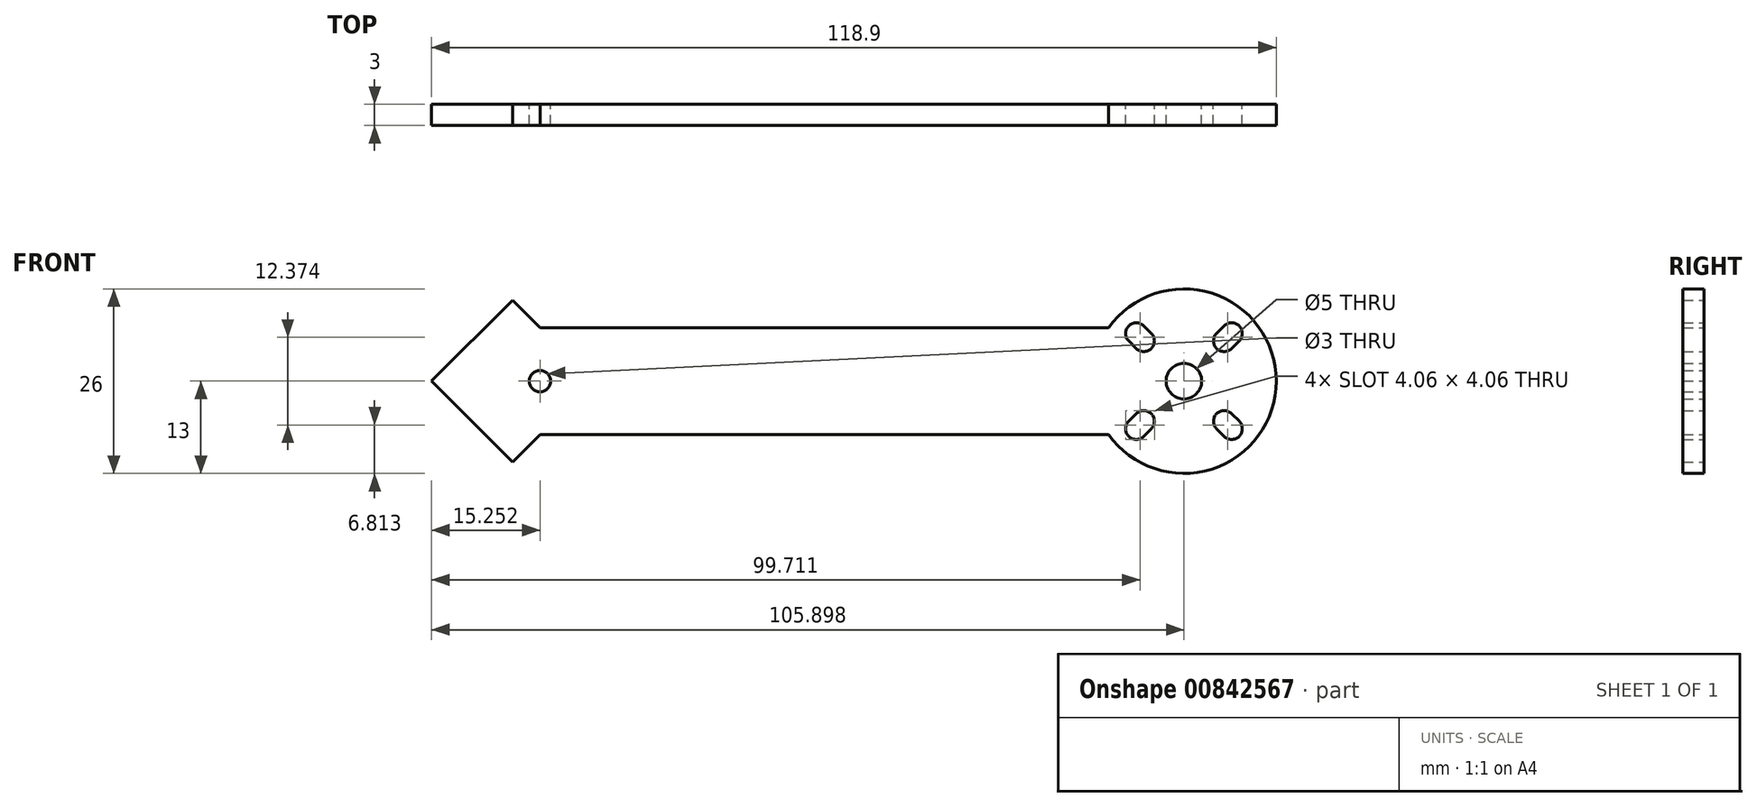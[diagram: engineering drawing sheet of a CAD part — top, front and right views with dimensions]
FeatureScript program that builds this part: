
annotation { "Feature Type Name" : "Feature", "Feature Type Description" : "" }
export const myFeature = defineFeature(function(context is Context, id is Id, definition is map)
    precondition{}
    {
        {
            var Q0;
            Q0=qCreatedBy(makeId("Front.planeOp"),FACE);
            var sketch = newSketch(context, id + "F0", { "sketchPlane" : qUnion([Q0])});
            skPoint(sketch, "E0.middle", {"position": v(0, 0) * mm});
            skLineSegment(sketch, "E1.bottom", {"start": v(0, 0) * mm, "end": v(80, 0) * mm});
            skLineSegment(sketch, "E1.top", {"start": v(0, 15) * mm, "end": v(80, 15) * mm});
            skLineSegment(sketch, "E1.left", {"start": v(0, 0) * mm, "end": v(0, 15) * mm});
            skLineSegment(sketch, "E1.right", {"start": v(80, 0) * mm, "end": v(80, 15) * mm});
            skCircle(sketch, "E2", {"center": v(90.62, 7.5) * mm, "radius": 13 * mm});
            skCircle(sketch, "E3", {"center": v(90.62, 7.5) * mm, "radius": 2.5 * mm});
            skLineSegment(sketch, "E4", {"start": v(0, 15) * mm, "end": v(-3.89, 18.89) * mm});
            skLineSegment(sketch, "E5", {"start": v(-3.89, 18.89) * mm, "end": v(-15.28, 7.5) * mm});
            skLineSegment(sketch, "E6", {"start": v(-15.28, 7.5) * mm, "end": v(-3.89, -3.89) * mm});
            skLineSegment(sketch, "E7", {"start": v(-3.89, -3.89) * mm, "end": v(0, 0) * mm});
            skLineSegment(sketch, "E8", {"start": v(90.62, 7.5) * mm, "end": v(81.43, 16.7) * mm});
            skLineSegment(sketch, "E9", {"start": v(90.62, 7.5) * mm, "end": v(99.81, 16.7) * mm});
            skLineSegment(sketch, "E10", {"start": v(80, 7.5) * mm, "end": v(90.62, 7.5) * mm});
            skCircle(sketch, "E11", {"center": v(83.9, 14.22) * mm, "radius": 1.5 * mm});
            skCircle(sketch, "E12", {"center": v(84.96, 13.16) * mm, "radius": 1.5 * mm});
            skLineSegment(sketch, "E13", {"start": v(84.96, 15.28) * mm, "end": v(86.02, 14.22) * mm});
            skLineSegment(sketch, "E14", {"start": v(82.84, 13.16) * mm, "end": v(83.9, 12.1) * mm});
            skCircle(sketch, "E15.MirrorC", {"center": v(84.96, 1.84) * mm, "radius": 1.5 * mm});
            skCircle(sketch, "E16.MirrorC", {"center": v(83.9, 0.78) * mm, "radius": 1.5 * mm});
            skLineSegment(sketch, "E17.MirrorCS", {"start": v(82.84, 1.84) * mm, "end": v(83.9, 2.9) * mm});
            skLineSegment(sketch, "E18.MirrorCS", {"start": v(84.96, -0.28) * mm, "end": v(86.02, 0.78) * mm});
            skCircle(sketch, "E19.MirrorC", {"center": v(96.28, 1.84) * mm, "radius": 1.5 * mm});
            skLineSegment(sketch, "E20.MirrorCS", {"start": v(98.4, 1.84) * mm, "end": v(97.34, 2.9) * mm});
            skLineSegment(sketch, "E21.MirrorCS", {"start": v(96.28, -0.28) * mm, "end": v(95.21, 0.78) * mm});
            skCircle(sketch, "E22.MirrorC", {"center": v(97.34, 0.78) * mm, "radius": 1.5 * mm});
            skCircle(sketch, "E23.MirrorC", {"center": v(96.28, 13.16) * mm, "radius": 1.5 * mm});
            skLineSegment(sketch, "E24.MirrorCS", {"start": v(98.4, 13.16) * mm, "end": v(97.34, 12.1) * mm});
            skLineSegment(sketch, "E25.MirrorCS", {"start": v(96.28, 15.28) * mm, "end": v(95.21, 14.22) * mm});
            skCircle(sketch, "E26.MirrorC", {"center": v(97.34, 14.22) * mm, "radius": 1.5 * mm});
            skLineSegment(sketch, "E27", {"start": v(-3.89, 18.89) * mm, "end": v(-3.89, -3.89) * mm});
            skLineSegment(sketch, "E28", {"start": v(-15.28, 7.5) * mm, "end": v(0, 7.5) * mm});
            skPoint(sketch, "E29", {"position": v(-0.03, 7.5) * mm});
            skCircle(sketch, "E30", {"center": v(-0.03, 7.5) * mm, "radius": 1.5 * mm});
            skSolve(sketch);
        }
        {
            var Q0;
            Q0 = qSketchRegion(id + "F0", true);
            extrude(context, id + "F1", {"entities" : qUnion([Q0]), "depth" : 3 * mm, "offsetDistance" : 25 * mm});
        }
    });
